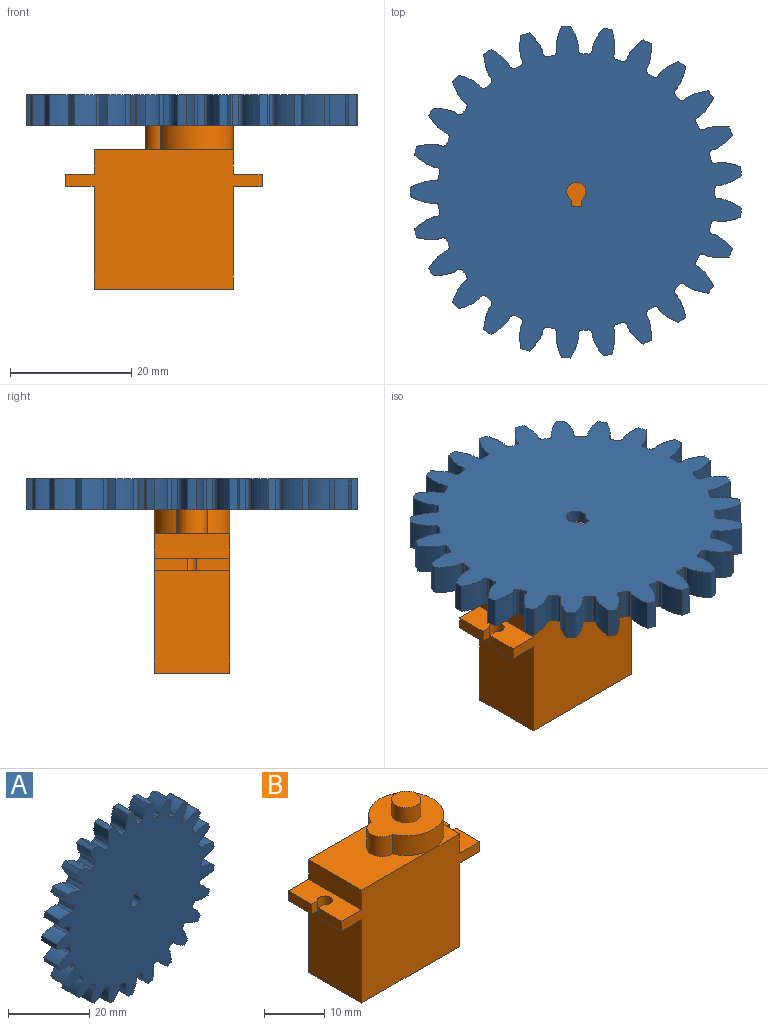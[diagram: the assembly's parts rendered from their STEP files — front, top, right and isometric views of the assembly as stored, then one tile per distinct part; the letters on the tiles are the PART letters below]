
ASSEMBLY  parts=2 mates=1
PART A: 156 faces, bbox 54.7x5.1x54.8 mm
  f0: cylinder r=27.43mm len=5.08mm, axis (0,1,0), area 7.4mm2, adj f24,f30,f141,f153
  f1: cylinder r=27.43mm len=5.08mm, axis (0,1,0), area 7.4mm2, adj f24,f30,f148,f151
  f2: cylinder r=27.43mm len=5.08mm, axis (0,1,0), area 7.4mm2, adj f24,f30,f136,f143
  f3: cylinder r=27.43mm len=5.08mm, axis (0,1,0), area 7.4mm2, adj f24,f30,f131,f138
  f4: cylinder r=27.43mm len=5.08mm, axis (0,1,0), area 7.4mm2, adj f24,f30,f126,f133
  f5: cylinder r=27.43mm len=5.08mm, axis (0,1,0), area 7.4mm2, adj f24,f30,f116,f128
  f6: cylinder r=27.43mm len=5.08mm, axis (0,1,0), area 7.4mm2, adj f24,f30,f111,f123
  f7: cylinder r=27.43mm len=5.08mm, axis (0,1,0), area 7.4mm2, adj f24,f30,f118,f121
  f8: cylinder r=27.43mm len=5.08mm, axis (0,1,0), area 7.4mm2, adj f24,f30,f106,f113
  f9: cylinder r=27.43mm len=5.08mm, axis (0,1,0), area 7.4mm2, adj f24,f30,f101,f108
  f10: cylinder r=27.43mm len=5.08mm, axis (0,1,0), area 7.4mm2, adj f24,f30,f96,f103
  f11: cylinder r=27.43mm len=5.08mm, axis (0,1,0), area 7.4mm2, adj f24,f30,f81,f98
  f12: cylinder r=27.43mm len=5.08mm, axis (0,1,0), area 7.4mm2, adj f24,f30,f31,f93
  f13: cylinder r=27.43mm len=5.08mm, axis (0,1,0), area 7.4mm2, adj f24,f30,f88,f91
  f14: cylinder r=27.43mm len=5.08mm, axis (0,1,0), area 7.4mm2, adj f24,f30,f76,f83
  f15: cylinder r=27.43mm len=5.08mm, axis (0,1,0), area 7.4mm2, adj f24,f30,f78,f86
  f16: cylinder r=27.43mm len=5.08mm, axis (0,1,0), area 7.4mm2, adj f24,f30,f73,f146
  f17: cylinder r=27.43mm len=5.08mm, axis (0,1,0), area 7.4mm2, adj f24,f30,f68,f71
  f18: cylinder r=27.43mm len=5.08mm, axis (0,1,0), area 7.4mm2, adj f24,f30,f63,f66
  f19: cylinder r=27.43mm len=5.08mm, axis (0,1,0), area 7.4mm2, adj f24,f30,f58,f61
  f20: cylinder r=27.43mm len=5.08mm, axis (0,1,0), area 7.4mm2, adj f24,f30,f46,f53
  f21: cylinder r=27.43mm len=5.08mm, axis (0,1,0), area 7.4mm2, adj f24,f30,f36,f48
  f22: cylinder r=27.43mm len=5.08mm, axis (0,1,0), area 7.4mm2, adj f24,f30,f43,f56
  f23: cylinder r=27.43mm len=5.08mm, axis (0,1,0), area 7.4mm2, adj f24,f30,f38,f41
  f24: plane 54.85x54.74mm, normal (0,-1,0), area 1985mm2, adj f0,f1,f2,f3,f4,f5,f6,f7
  f25: plane 5.08x1.01mm, normal (-1,0,0), area 5.1mm2, adj f24,f26,f28,f30
  f26: cylinder r=1.59mm len=5.08mm, axis (0,1,0), area 42.2mm2, adj f24,f25,f27,f30
  f27: plane 5.08x1.01mm, normal (1,0,0), area 5.1mm2, adj f24,f26,f28,f30
  f28: plane 5.08x1.59mm, normal (0,0,-1), area 8.1mm2, adj f24,f25,f27,f30
  f29: cylinder r=27.43mm len=5.08mm, axis (0,1,0), area 7.4mm2, adj f24,f30,f33,f51
  f30: plane 54.85x54.74mm, normal (0,1,0), area 1985mm2, adj f0,f1,f2,f3,f4,f5,f6,f7
  f31: extruded ~5.08x3.89mm, area 21.7mm2, adj f12,f24,f30,f34
  f32: cylinder r=22.86mm len=5.08mm, axis (0,1,0), area 5.4mm2, adj f24,f30,f34,f35
  f33: extruded ~5.08x3.89mm, area 21.7mm2, adj f24,f29,f30,f35
  f34: cylinder r=0.58mm len=5.08mm, axis (0,1,0), area 4.5mm2, adj f24,f30,f31,f32
  f35: cylinder r=0.58mm len=5.08mm, axis (0,1,0), area 4.5mm2, adj f24,f30,f32,f33
  f36: extruded ~5.08x3.93mm, area 21.7mm2, adj f21,f24,f30,f39
  f37: cylinder r=22.86mm len=5.08mm, axis (0,1,0), area 5.4mm2, adj f24,f30,f39,f40
  f38: extruded ~5.08x3.83mm, area 21.7mm2, adj f23,f24,f30,f40
  f39: cylinder r=0.58mm len=5.08mm, axis (0,1,0), area 4.5mm2, adj f24,f30,f36,f37
  f40: cylinder r=0.58mm len=5.08mm, axis (0,1,0), area 4.5mm2, adj f24,f30,f37,f38
  f41: extruded ~5.08x3.43mm, area 21.7mm2, adj f23,f24,f30,f44
  f42: cylinder r=22.86mm len=5.08mm, axis (0,1,0), area 5.4mm2, adj f24,f30,f44,f45
  f43: extruded ~5.08x4.14mm, area 21.7mm2, adj f22,f24,f30,f45
  f44: cylinder r=0.58mm len=5.08mm, axis (0,1,0), area 4.5mm2, adj f24,f30,f41,f42
  f45: cylinder r=0.58mm len=5.08mm, axis (0,1,0), area 4.5mm2, adj f24,f30,f42,f43
  f46: extruded ~5.08x4.18mm, area 21.7mm2, adj f20,f24,f30,f49
  f47: cylinder r=22.86mm len=5.08mm, axis (0,1,0), area 5.4mm2, adj f24,f30,f49,f50
  f48: extruded ~5.08x3.27mm, area 21.7mm2, adj f21,f24,f30,f50
  f49: cylinder r=0.58mm len=5.08mm, axis (0,1,0), area 4.5mm2, adj f24,f30,f46,f47
  f50: cylinder r=0.58mm len=5.08mm, axis (0,1,0), area 4.5mm2, adj f24,f30,f47,f48
  f51: extruded ~5.08x4.17mm, area 21.7mm2, adj f24,f29,f30,f54
  f52: cylinder r=22.86mm len=5.08mm, axis (0,1,0), area 5.4mm2, adj f24,f30,f54,f55
  f53: extruded ~5.08x3.38mm, area 21.7mm2, adj f20,f24,f30,f55
  f54: cylinder r=0.58mm len=5.08mm, axis (0,1,0), area 4.5mm2, adj f24,f30,f51,f52
  f55: cylinder r=0.58mm len=5.08mm, axis (0,1,0), area 4.5mm2, adj f24,f30,f52,f53
  f56: extruded ~5.08x3.21mm, area 21.7mm2, adj f22,f24,f30,f59
  f57: cylinder r=22.86mm len=5.08mm, axis (0,1,0), area 5.4mm2, adj f24,f30,f59,f60
  f58: extruded ~5.08x4.2mm, area 21.7mm2, adj f19,f24,f30,f60
  f59: cylinder r=0.58mm len=5.08mm, axis (0,1,0), area 4.5mm2, adj f24,f30,f56,f57
  f60: cylinder r=0.58mm len=5.08mm, axis (0,1,0), area 4.5mm2, adj f24,f30,f57,f58
  f61: extruded ~5.08x3.79mm, area 21.7mm2, adj f19,f24,f30,f64
  f62: cylinder r=22.86mm len=5.08mm, axis (0,1,0), area 5.4mm2, adj f24,f30,f64,f65
  f63: extruded ~5.08x3.99mm, area 21.7mm2, adj f18,f24,f30,f65
  f64: cylinder r=0.58mm len=5.08mm, axis (0,1,0), area 4.5mm2, adj f24,f30,f61,f62
  f65: cylinder r=0.58mm len=5.08mm, axis (0,1,0), area 4.5mm2, adj f24,f30,f62,f63
  f66: extruded ~5.08x4.12mm, area 21.7mm2, adj f18,f24,f30,f69
  f67: cylinder r=22.86mm len=5.08mm, axis (0,1,0), area 5.4mm2, adj f24,f30,f69,f70
  f68: extruded ~5.08x3.53mm, area 21.7mm2, adj f17,f24,f30,f70
  f69: cylinder r=0.58mm len=5.08mm, axis (0,1,0), area 4.5mm2, adj f24,f30,f66,f67
  f70: cylinder r=0.58mm len=5.08mm, axis (0,1,0), area 4.5mm2, adj f24,f30,f67,f68
  f71: extruded ~5.08x4.2mm, area 21.7mm2, adj f17,f24,f30,f74
  f72: cylinder r=22.86mm len=5.08mm, axis (0,1,0), area 5.4mm2, adj f24,f30,f74,f75
  f73: extruded ~5.08x3.1mm, area 21.7mm2, adj f16,f24,f30,f75
  f74: cylinder r=0.58mm len=5.08mm, axis (0,1,0), area 4.5mm2, adj f24,f30,f71,f72
  f75: cylinder r=0.58mm len=5.08mm, axis (0,1,0), area 4.5mm2, adj f24,f30,f72,f73
  f76: extruded ~5.08x3.83mm, area 21.7mm2, adj f14,f24,f30,f79
  f77: cylinder r=22.86mm len=5.08mm, axis (0,1,0), area 5.4mm2, adj f24,f30,f79,f80
  f78: extruded ~5.08x3.93mm, area 21.7mm2, adj f15,f24,f30,f80
  f79: cylinder r=0.58mm len=5.08mm, axis (0,1,0), area 4.5mm2, adj f24,f30,f76,f77
  f80: cylinder r=0.58mm len=5.08mm, axis (0,1,0), area 4.5mm2, adj f24,f30,f77,f78
  f81: extruded ~5.08x4.14mm, area 21.7mm2, adj f11,f24,f30,f84
  f82: cylinder r=22.86mm len=5.08mm, axis (0,1,0), area 5.4mm2, adj f24,f30,f84,f85
  f83: extruded ~5.08x3.43mm, area 21.7mm2, adj f14,f24,f30,f85
  f84: cylinder r=0.58mm len=5.08mm, axis (0,1,0), area 4.5mm2, adj f24,f30,f81,f82
  f85: cylinder r=0.58mm len=5.08mm, axis (0,1,0), area 4.5mm2, adj f24,f30,f82,f83
  f86: extruded ~5.08x3.27mm, area 21.7mm2, adj f15,f24,f30,f89
  f87: cylinder r=22.86mm len=5.08mm, axis (0,1,0), area 5.4mm2, adj f24,f30,f89,f90
  f88: extruded ~5.08x4.18mm, area 21.7mm2, adj f13,f24,f30,f90
  f89: cylinder r=0.58mm len=5.08mm, axis (0,1,0), area 4.5mm2, adj f24,f30,f86,f87
  f90: cylinder r=0.58mm len=5.08mm, axis (0,1,0), area 4.5mm2, adj f24,f30,f87,f88
  f91: extruded ~5.08x3.38mm, area 21.7mm2, adj f13,f24,f30,f94
  f92: cylinder r=22.86mm len=5.08mm, axis (0,1,0), area 5.4mm2, adj f24,f30,f94,f95
  f93: extruded ~5.08x4.17mm, area 21.7mm2, adj f12,f24,f30,f95
  f94: cylinder r=0.58mm len=5.08mm, axis (0,1,0), area 4.5mm2, adj f24,f30,f91,f92
  f95: cylinder r=0.58mm len=5.08mm, axis (0,1,0), area 4.5mm2, adj f24,f30,f92,f93
  f96: extruded ~5.08x4.2mm, area 21.7mm2, adj f10,f24,f30,f99
  f97: cylinder r=22.86mm len=5.08mm, axis (0,1,0), area 5.4mm2, adj f24,f30,f99,f100
  f98: extruded ~5.08x3.21mm, area 21.7mm2, adj f11,f24,f30,f100
  f99: cylinder r=0.58mm len=5.08mm, axis (0,1,0), area 4.5mm2, adj f24,f30,f96,f97
  f100: cylinder r=0.58mm len=5.08mm, axis (0,1,0), area 4.5mm2, adj f24,f30,f97,f98
  f101: extruded ~5.08x3.99mm, area 21.7mm2, adj f9,f24,f30,f104
  f102: cylinder r=22.86mm len=5.08mm, axis (0,1,0), area 5.4mm2, adj f24,f30,f104,f105
  f103: extruded ~5.08x3.79mm, area 21.7mm2, adj f10,f24,f30,f105
  f104: cylinder r=0.58mm len=5.08mm, axis (0,1,0), area 4.5mm2, adj f24,f30,f101,f102
  f105: cylinder r=0.58mm len=5.08mm, axis (0,1,0), area 4.5mm2, adj f24,f30,f102,f103
  f106: extruded ~5.08x3.53mm, area 21.7mm2, adj f8,f24,f30,f109
  f107: cylinder r=22.86mm len=5.08mm, axis (0,1,0), area 5.4mm2, adj f24,f30,f109,f110
  f108: extruded ~5.08x4.12mm, area 21.7mm2, adj f9,f24,f30,f110
  f109: cylinder r=0.58mm len=5.08mm, axis (0,1,0), area 4.5mm2, adj f24,f30,f106,f107
  f110: cylinder r=0.58mm len=5.08mm, axis (0,1,0), area 4.5mm2, adj f24,f30,f107,f108
  f111: extruded ~5.08x3.1mm, area 21.7mm2, adj f6,f24,f30,f114
  f112: cylinder r=22.86mm len=5.08mm, axis (0,1,0), area 5.4mm2, adj f24,f30,f114,f115
  f113: extruded ~5.08x4.2mm, area 21.7mm2, adj f8,f24,f30,f115
  f114: cylinder r=0.58mm len=5.08mm, axis (0,1,0), area 4.5mm2, adj f24,f30,f111,f112
  f115: cylinder r=0.58mm len=5.08mm, axis (0,1,0), area 4.5mm2, adj f24,f30,f112,f113
  f116: extruded ~5.08x4.09mm, area 21.7mm2, adj f5,f24,f30,f119
  f117: cylinder r=22.86mm len=5.08mm, axis (0,1,0), area 5.4mm2, adj f24,f30,f119,f120
  f118: extruded ~5.08x3.58mm, area 21.7mm2, adj f7,f24,f30,f120
  f119: cylinder r=0.58mm len=5.08mm, axis (0,1,0), area 4.5mm2, adj f24,f30,f116,f117
  f120: cylinder r=0.58mm len=5.08mm, axis (0,1,0), area 4.5mm2, adj f24,f30,f117,f118
  f121: extruded ~5.08x3.71mm, area 21.7mm2, adj f7,f24,f30,f124
  f122: cylinder r=22.86mm len=5.08mm, axis (0,1,0), area 5.4mm2, adj f24,f30,f124,f125
  f123: extruded ~5.08x4.02mm, area 21.7mm2, adj f6,f24,f30,f125
  f124: cylinder r=0.58mm len=5.08mm, axis (0,1,0), area 4.5mm2, adj f24,f30,f121,f122
  f125: cylinder r=0.58mm len=5.08mm, axis (0,1,0), area 4.5mm2, adj f24,f30,f122,f123
  f126: extruded ~5.08x4.21mm, area 21.7mm2, adj f4,f24,f30,f129
  f127: cylinder r=22.86mm len=5.08mm, axis (0,1,0), area 5.4mm2, adj f24,f30,f129,f130
  f128: extruded ~5.08x3.03mm, area 21.7mm2, adj f5,f24,f30,f130
  f129: cylinder r=0.58mm len=5.08mm, axis (0,1,0), area 4.5mm2, adj f24,f30,f126,f127
  f130: cylinder r=0.58mm len=5.08mm, axis (0,1,0), area 4.5mm2, adj f24,f30,f127,f128
  f131: extruded ~5.08x4.06mm, area 21.7mm2, adj f3,f24,f30,f134
  f132: cylinder r=22.86mm len=5.08mm, axis (0,1,0), area 5.4mm2, adj f24,f30,f134,f135
  f133: extruded ~5.08x3.66mm, area 21.7mm2, adj f4,f24,f30,f135
  f134: cylinder r=0.58mm len=5.08mm, axis (0,1,0), area 4.5mm2, adj f24,f30,f131,f132
  f135: cylinder r=0.58mm len=5.08mm, axis (0,1,0), area 4.5mm2, adj f24,f30,f132,f133
  f136: extruded ~5.08x3.66mm, area 21.7mm2, adj f2,f24,f30,f139
  f137: cylinder r=22.86mm len=5.08mm, axis (0,1,0), area 5.4mm2, adj f24,f30,f139,f140
  f138: extruded ~5.08x4.06mm, area 21.7mm2, adj f3,f24,f30,f140
  f139: cylinder r=0.58mm len=5.08mm, axis (0,1,0), area 4.5mm2, adj f24,f30,f136,f137
  f140: cylinder r=0.58mm len=5.08mm, axis (0,1,0), area 4.5mm2, adj f24,f30,f137,f138
  f141: extruded ~5.08x3.03mm, area 21.7mm2, adj f0,f24,f30,f144
  f142: cylinder r=22.86mm len=5.08mm, axis (0,1,0), area 5.4mm2, adj f24,f30,f144,f145
  f143: extruded ~5.08x4.21mm, area 21.7mm2, adj f2,f24,f30,f145
  f144: cylinder r=0.58mm len=5.08mm, axis (0,1,0), area 4.5mm2, adj f24,f30,f141,f142
  f145: cylinder r=0.58mm len=5.08mm, axis (0,1,0), area 4.5mm2, adj f24,f30,f142,f143
  f146: extruded ~5.08x4.02mm, area 21.7mm2, adj f16,f24,f30,f149
  f147: cylinder r=22.86mm len=5.08mm, axis (0,1,0), area 5.4mm2, adj f24,f30,f149,f150
  f148: extruded ~5.08x3.71mm, area 21.7mm2, adj f1,f24,f30,f150
  f149: cylinder r=0.58mm len=5.08mm, axis (0,1,0), area 4.5mm2, adj f24,f30,f146,f147
  f150: cylinder r=0.58mm len=5.08mm, axis (0,1,0), area 4.5mm2, adj f24,f30,f147,f148
  f151: extruded ~5.08x3.58mm, area 21.7mm2, adj f1,f24,f30,f154
  f152: cylinder r=22.86mm len=5.08mm, axis (0,1,0), area 5.4mm2, adj f24,f30,f154,f155
  f153: extruded ~5.08x4.09mm, area 21.7mm2, adj f0,f24,f30,f155
  f154: cylinder r=0.58mm len=5.08mm, axis (0,1,0), area 4.5mm2, adj f24,f30,f151,f152
  f155: cylinder r=0.58mm len=5.08mm, axis (0,1,0), area 4.5mm2, adj f24,f30,f152,f153
PART B: 29 faces, bbox 32.5x12.6x30 mm
  f0: plane 4.99x4.9mm, normal (0,0,1), area 18.9mm2, adj f1
  f1: cylinder r=2.45mm len=4.9mm, axis (0,0,1), area 46.2mm2, adj f0,f2
  f2: plane 14.61x12.65mm, normal (0,0,1), area 112mm2, adj f1,f3,f4
  f3: cylinder r=2.5mm len=5mm, axis (0,0,1), area 31.6mm2, adj f2,f4,f10
  f4: cylinder r=6.25mm len=12.5mm, axis (0,0,1), area 136.5mm2, adj f2,f3,f8,f10,f11
  f5: plane 2x1.38mm, normal (0,-1,0), area 2.7mm2, adj f6,f9,f13,f15
  f6: cylinder r=1.25mm len=2.5mm, axis (0,0,-1), area 12.5mm2, adj f5,f7,f13,f15
  f7: plane 2x1.38mm, normal (0,1,0), area 2.7mm2, adj f6,f13,f14,f15
  f8: plane 6.25x6.25mm, normal (0,0,1), area 8.4mm2, adj f4,f12,f20
  f9: plane 5.5x2mm, normal (1,0,0), area 11mm2, adj f5,f13,f15,f20
  f10: plane 16.75x12.5mm, normal (0,0,1), area 139.8mm2, adj f3,f4,f18,f20,f22
  f11: plane 6.25x6.25mm, normal (0,0,1), area 8.4mm2, adj f4,f12,f22
  f12: plane 12.5x4mm, normal (1,0,0), area 50mm2, adj f8,f11,f13,f20,f22
  f13: plane 12.5x4.75mm, normal (0,0,1), area 52.7mm2, adj f5,f6,f7,f9,f12,f14,f20,f22
  f14: plane 5.5x2mm, normal (1,0,0), area 11mm2, adj f7,f13,f15,f22
  f15: plane 12.5x4.75mm, normal (0,0,-1), area 52.7mm2, adj f5,f6,f7,f9,f14,f16,f20,f22
  f16: plane 17x12.5mm, normal (1,0,0), area 212.5mm2, adj f15,f17,f20,f22
  f17: plane 23x12.5mm, normal (0,0,-1), area 287.5mm2, adj f16,f20,f21,f22
  f18: plane 12.5x4mm, normal (-1,0,0), area 50mm2, adj f10,f20,f22,f25
  f19: plane 5.5x2mm, normal (-1,0,0), area 11mm2, adj f20,f24,f25,f27
  f20: plane 32.5x23mm, normal (0,1,0), area 548mm2, adj f8,f9,f10,f12,f13,f15,f16,f17
  f21: plane 17x12.5mm, normal (-1,0,0), area 212.5mm2, adj f17,f20,f22,f27
  f22: plane 32.5x23mm, normal (0,-1,0), area 548mm2, adj f10,f11,f12,f13,f14,f15,f16,f17
  f23: plane 5.5x2mm, normal (-1,0,0), area 11mm2, adj f22,f25,f26,f27
  f24: plane 2x1.38mm, normal (0,-1,0), area 2.8mm2, adj f19,f25,f27,f28
  f25: plane 12.5x4.75mm, normal (0,0,1), area 52.7mm2, adj f18,f19,f20,f22,f23,f24,f26,f28
  f26: plane 2x1.38mm, normal (0,1,0), area 2.8mm2, adj f23,f25,f27,f28
  f27: plane 12.5x4.75mm, normal (0,0,-1), area 52.7mm2, adj f19,f20,f21,f22,f23,f24,f26,f28
  f28: cylinder r=1.25mm len=2.5mm, axis (0,0,-1), area 12.5mm2, adj f24,f25,f26,f27
PLACE A rot(axis=(1,0,0),90deg) t=(11.2,10.77,27.64)mm
PLACE B t=(17.96,4.52,-4.44)mm
MATE fastened A.f0 <-> B.f2  axis (0,0,-1) through (11.2,10.77,22.56)mm
